# Revit family: 0971212_BSCH
name_source: partatom
category: Air Terminals
revit_build: Autodesk Revit MEP 2012 (Build: 20110309_2315(x64)
units: mm (PartAtom-declared; Revit-internal decimal feet)

## types (1)
- BSCH
    Conect_H = 17 3/4"
    Conect_V = 17 3/4"
    Cuello Cuadrado Mín-Máx = Desde 8"x8" hasta 18"x18"
    Cuello Rectangular Mín-Máx = Desde 10"x8" hasta 18"x16"
    Description = Rejilla de inyección
    Función = Inyección
    Incrementos de cuello = de 2"
    Manufacturer = INNES
    Material = Aluminio/Acero
    Medida_Requerida_Horizontal = 18"
    Medida_Requerida_Vertical = 18"
    Model = BSCH
    No. de vías disponibles = 1, 2, 3 y 4
    Nota1 = .
    N°_De_Vias = 2
    Posición de Instalación = Muro/Techo
    Posición de aletas = Horizontal
    Tipo de Cuello = Rectangular
    Type Comments = Configuración en: 1, 2, 3, ó 4 vías
    URL = https://www.innes.com.mx
    Var_H = 18"
    Var_V = 18"
    Visible_Texto = No

## geometry (parser evidence)
native form markers: Sweep x14
no freeform markers — native parametric forms only
